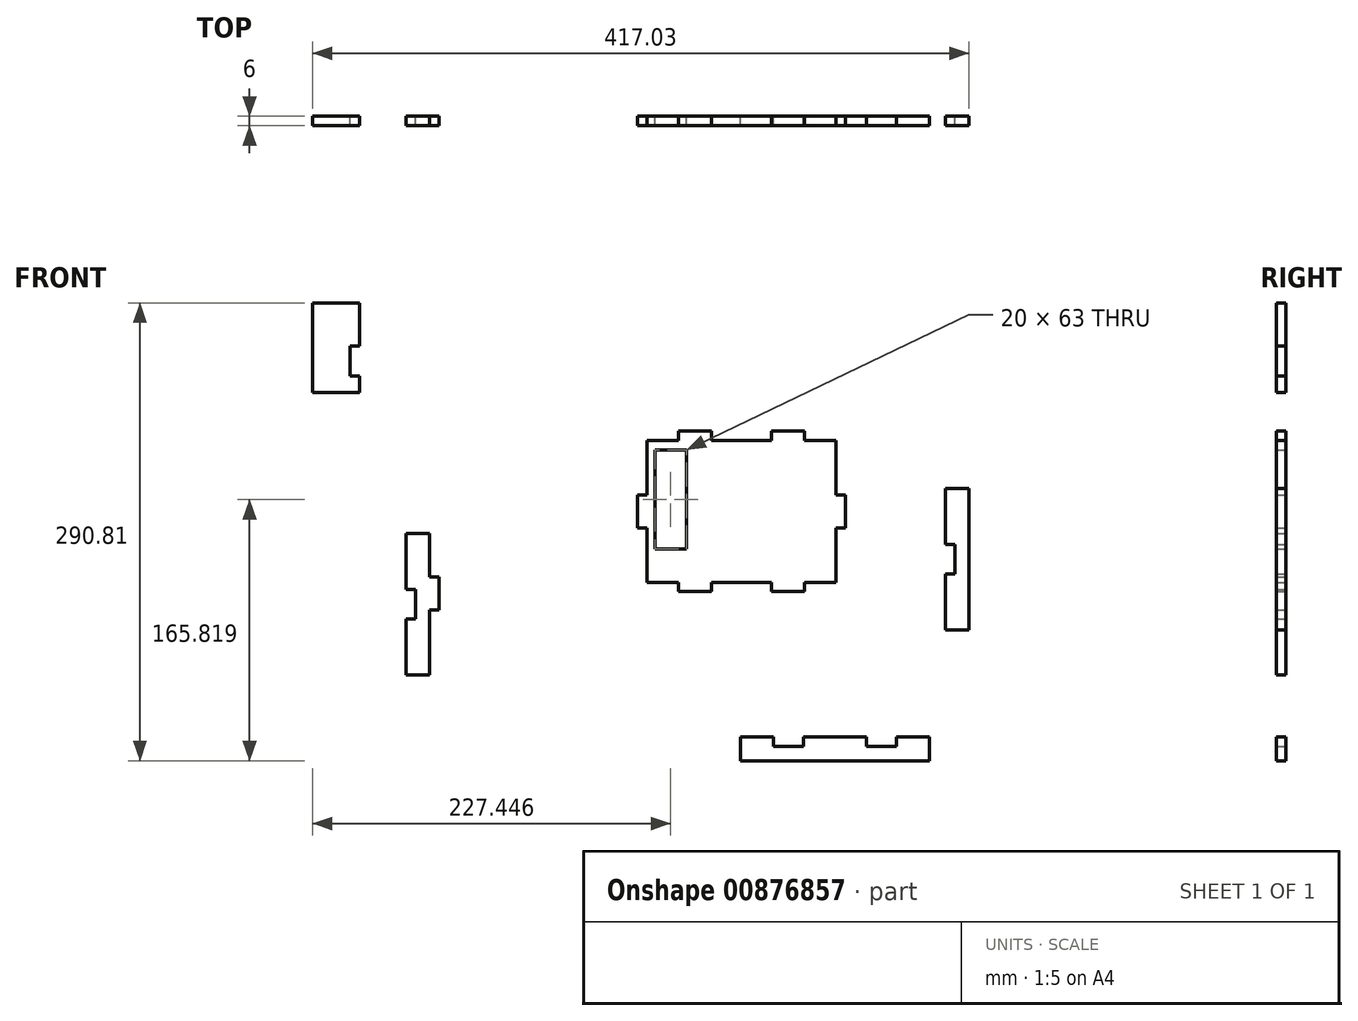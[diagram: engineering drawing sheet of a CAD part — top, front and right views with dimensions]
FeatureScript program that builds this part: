
annotation { "Feature Type Name" : "Feature", "Feature Type Description" : "" }
export const myFeature = defineFeature(function(context is Context, id is Id, definition is map)
    precondition{}
    {
        {
            var Q0;
            Q0=qCreatedBy(makeId("Front.planeOp"),FACE);
            var sketch = newSketch(context, id + "F0", { "sketchPlane" : qUnion([Q0])});
            skLineSegment(sketch, "E0", {"start": v(-67.51, 70.89) * mm, "end": v(-47.51, 70.89) * mm});
            skLineSegment(sketch, "E1", {"start": v(-67.51, 70.89) * mm, "end": v(-67.51, 36.34) * mm});
            skLineSegment(sketch, "E2", {"start": v(-67.51, -19.11) * mm, "end": v(-47.51, -19.11) * mm});
            skLineSegment(sketch, "E3", {"start": v(52.49, -19.11) * mm, "end": v(52.49, 15.44) * mm});
            skLineSegment(sketch, "E4", {"start": v(-47.51, 70.89) * mm, "end": v(-47.51, 76.89) * mm});
            skLineSegment(sketch, "E5", {"start": v(-47.51, 76.89) * mm, "end": v(-26.61, 76.89) * mm});
            skLineSegment(sketch, "E6", {"start": v(-26.61, 76.89) * mm, "end": v(-26.61, 70.89) * mm});
            skLineSegment(sketch, "E7", {"start": v(32.49, 70.89) * mm, "end": v(32.49, 76.89) * mm});
            skLineSegment(sketch, "E8", {"start": v(32.49, 76.89) * mm, "end": v(11.59, 76.89) * mm});
            skLineSegment(sketch, "E9", {"start": v(11.59, 76.89) * mm, "end": v(11.59, 70.89) * mm});
            skLineSegment(sketch, "E10.bottom", {"start": v(-8.1, -117.43) * mm, "end": v(12.9, -117.43) * mm});
            skLineSegment(sketch, "E10.top", {"start": v(-8.1, -132.43) * mm, "end": v(111.9, -132.43) * mm});
            skLineSegment(sketch, "E10.left", {"start": v(-8.1, -117.43) * mm, "end": v(-8.1, -132.43) * mm});
            skLineSegment(sketch, "E10.right", {"start": v(111.9, -117.43) * mm, "end": v(111.9, -132.43) * mm});
            skLineSegment(sketch, "E11", {"start": v(12.9, -117.43) * mm, "end": v(12.9, -123.43) * mm});
            skLineSegment(sketch, "E12", {"start": v(12.9, -123.43) * mm, "end": v(31.8, -123.43) * mm});
            skLineSegment(sketch, "E13", {"start": v(31.8, -123.43) * mm, "end": v(31.8, -117.43) * mm});
            skLineSegment(sketch, "E14", {"start": v(90.9, -117.43) * mm, "end": v(90.9, -123.43) * mm});
            skLineSegment(sketch, "E15", {"start": v(90.9, -123.43) * mm, "end": v(72, -123.43) * mm});
            skLineSegment(sketch, "E16", {"start": v(72, -123.43) * mm, "end": v(72, -117.43) * mm});
            skLineSegment(sketch, "E17", {"start": v(-73.51, 36.34) * mm, "end": v(-73.51, 15.44) * mm});
            skLineSegment(sketch, "E18", {"start": v(-73.51, 15.44) * mm, "end": v(-67.51, 15.44) * mm});
            skLineSegment(sketch, "E19.MirrorCS", {"start": v(58.49, 36.34) * mm, "end": v(58.49, 15.44) * mm});
            skLineSegment(sketch, "E20.MirrorCS", {"start": v(58.49, 15.44) * mm, "end": v(52.49, 15.44) * mm});
            skLineSegment(sketch, "E21.MirrorCS", {"start": v(52.49, 36.34) * mm, "end": v(58.49, 36.34) * mm});
            skLineSegment(sketch, "E22", {"start": v(51.9, -117.43) * mm, "end": v(51.9, -132.43) * mm, "construction": true});
            skLineSegment(sketch, "E23.MirrorCS", {"start": v(-47.51, -19.11) * mm, "end": v(-47.51, -25.11) * mm});
            skLineSegment(sketch, "E24.MirrorCS", {"start": v(-26.61, -25.11) * mm, "end": v(-26.61, -19.11) * mm});
            skLineSegment(sketch, "E25.MirrorCS", {"start": v(32.49, -19.11) * mm, "end": v(32.49, -25.11) * mm});
            skLineSegment(sketch, "E26", {"start": v(137.07, 40.56) * mm, "end": v(137.07, -49.44) * mm});
            skLineSegment(sketch, "E27", {"start": v(137.07, -49.44) * mm, "end": v(122.07, -49.44) * mm});
            skLineSegment(sketch, "E28", {"start": v(137.07, 40.56) * mm, "end": v(122.07, 40.56) * mm});
            skLineSegment(sketch, "E29", {"start": v(122.07, 40.56) * mm, "end": v(122.07, 5) * mm});
            skLineSegment(sketch, "E30", {"start": v(122.07, 5) * mm, "end": v(128.07, 5) * mm});
            skLineSegment(sketch, "E31", {"start": v(128.07, 5) * mm, "end": v(128.07, -13.9) * mm});
            skLineSegment(sketch, "E32", {"start": v(128.07, -13.9) * mm, "end": v(122.07, -13.9) * mm});
            skLineSegment(sketch, "E33.trimOffspring", {"start": v(-26.61, 70.89) * mm, "end": v(11.59, 70.89) * mm});
            skLineSegment(sketch, "E34.trimOffspring", {"start": v(32.49, 70.89) * mm, "end": v(52.49, 70.89) * mm});
            skLineSegment(sketch, "E35.trimOffspring", {"start": v(-67.51, 15.44) * mm, "end": v(-67.51, -19.11) * mm});
            skLineSegment(sketch, "E36.trimOffspring", {"start": v(52.49, 36.34) * mm, "end": v(52.49, 70.89) * mm});
            skLineSegment(sketch, "E37.trimOffspring", {"start": v(-26.61, -19.11) * mm, "end": v(11.59, -19.11) * mm});
            skLineSegment(sketch, "E38.trimOffspring", {"start": v(32.49, -19.11) * mm, "end": v(52.49, -19.11) * mm});
            skLineSegment(sketch, "E39.trimOffspring", {"start": v(122.07, -13.9) * mm, "end": v(122.07, -49.44) * mm});
            skLineSegment(sketch, "E40.trimOffspring", {"start": v(90.9, -117.43) * mm, "end": v(111.9, -117.43) * mm});
            skLineSegment(sketch, "E41.trimOffspring", {"start": v(31.8, -117.43) * mm, "end": v(72, -117.43) * mm});
            skLineSegment(sketch, "E42", {"start": v(-205.46, 11.9) * mm, "end": v(-205.46, -15.66) * mm});
            skLineSegment(sketch, "E43", {"start": v(-205.46, -78.1) * mm, "end": v(-220.46, -78.1) * mm});
            skLineSegment(sketch, "E44", {"start": v(-205.46, 11.9) * mm, "end": v(-220.46, 11.9) * mm});
            skLineSegment(sketch, "E45", {"start": v(-220.46, 11.9) * mm, "end": v(-220.46, -23.66) * mm});
            skLineSegment(sketch, "E46", {"start": v(-220.46, -23.66) * mm, "end": v(-214.46, -23.66) * mm});
            skLineSegment(sketch, "E47", {"start": v(-214.46, -23.66) * mm, "end": v(-214.46, -42.56) * mm});
            skLineSegment(sketch, "E48", {"start": v(-214.46, -42.56) * mm, "end": v(-220.46, -42.56) * mm});
            skLineSegment(sketch, "E49.trimOffspring", {"start": v(-220.46, -42.56) * mm, "end": v(-220.46, -78.1) * mm});
            skLineSegment(sketch, "E50", {"start": v(-205.46, -15.66) * mm, "end": v(-199.46, -15.66) * mm});
            skLineSegment(sketch, "E51", {"start": v(-199.46, -15.66) * mm, "end": v(-199.46, -36.56) * mm});
            skLineSegment(sketch, "E52", {"start": v(-199.46, -36.56) * mm, "end": v(-205.46, -36.56) * mm});
            skLineSegment(sketch, "E53", {"start": v(-67.51, 36.34) * mm, "end": v(-73.51, 36.34) * mm});
            skLineSegment(sketch, "E54.trimOffspring", {"start": v(-205.46, -36.56) * mm, "end": v(-205.46, -78.1) * mm});
            skLineSegment(sketch, "E55", {"start": v(-279.96, 158.38) * mm, "end": v(-249.96, 158.38) * mm});
            skLineSegment(sketch, "E56", {"start": v(-249.96, 158.38) * mm, "end": v(-249.96, 130.83) * mm});
            skLineSegment(sketch, "E57", {"start": v(-249.96, 101.38) * mm, "end": v(-279.96, 101.38) * mm});
            skLineSegment(sketch, "E58", {"start": v(-279.96, 101.38) * mm, "end": v(-279.96, 158.38) * mm});
            skLineSegment(sketch, "E59", {"start": v(-249.96, 130.83) * mm, "end": v(-255.96, 130.83) * mm});
            skLineSegment(sketch, "E60", {"start": v(-255.96, 130.83) * mm, "end": v(-255.96, 111.93) * mm});
            skLineSegment(sketch, "E61", {"start": v(-255.96, 111.93) * mm, "end": v(-249.96, 111.93) * mm});
            skLineSegment(sketch, "E62.trimOffspring", {"start": v(-249.96, 111.93) * mm, "end": v(-249.96, 101.38) * mm});
            skLineSegment(sketch, "E63.bottom", {"start": v(-62.51, 64.89) * mm, "end": v(-42.51, 64.89) * mm});
            skLineSegment(sketch, "E63.top", {"start": v(-62.51, 1.89) * mm, "end": v(-42.51, 1.89) * mm});
            skLineSegment(sketch, "E63.left", {"start": v(-62.51, 64.89) * mm, "end": v(-62.51, 1.89) * mm});
            skLineSegment(sketch, "E63.right", {"start": v(-42.51, 64.89) * mm, "end": v(-42.51, 1.89) * mm});
            skLineSegment(sketch, "E64", {"start": v(11.59, -19.11) * mm, "end": v(11.59, -25.11) * mm});
            skLineSegment(sketch, "E65", {"start": v(-47.51, -25.11) * mm, "end": v(-26.61, -25.11) * mm});
            skLineSegment(sketch, "E66", {"start": v(11.59, -25.11) * mm, "end": v(32.49, -25.11) * mm});
            skSolve(sketch);
        }
        {
            var Q0;
            Q0 = qSketchRegion(id + "F0", true);
            extrude(context, id + "F1", {"entities" : qUnion([Q0]), "depth" : 6 * mm, "offsetDistance" : 25 * mm});
        }
    });
